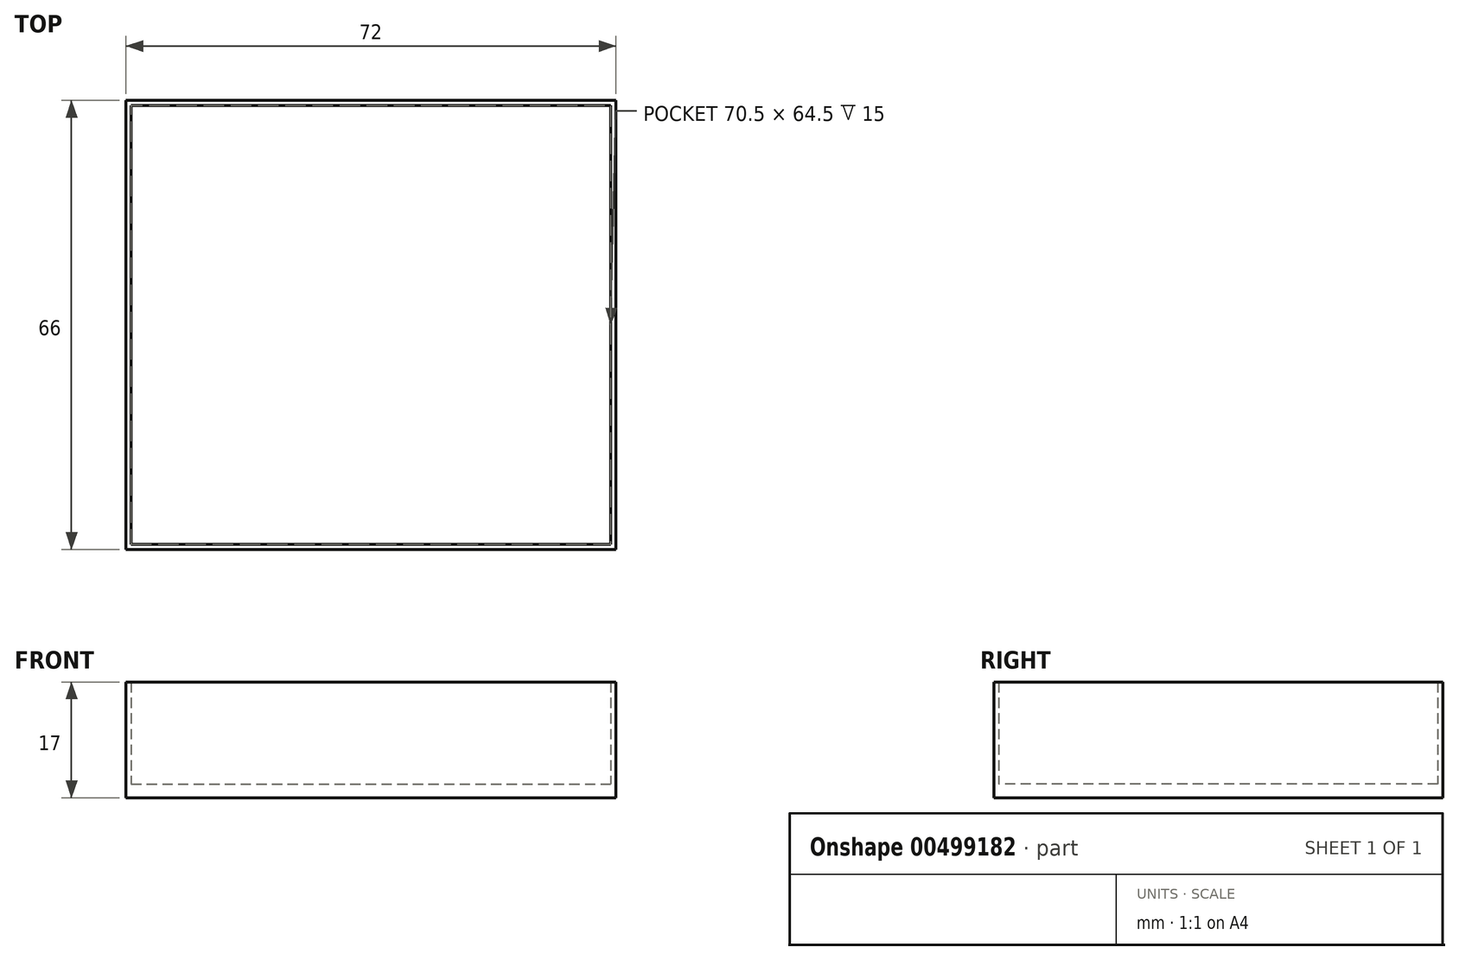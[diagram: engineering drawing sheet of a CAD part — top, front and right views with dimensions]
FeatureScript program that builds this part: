
annotation { "Feature Type Name" : "Feature", "Feature Type Description" : "" }
export const myFeature = defineFeature(function(context is Context, id is Id, definition is map)
    precondition{}
    {
        {
            var Q0;
            Q0=qCreatedBy(makeId("Top.planeOp"),FACE);
            var sketch = newSketch(context, id + "F0", { "sketchPlane" : qUnion([Q0])});
            skLineSegment(sketch, "E0.bottom", {"start": v(-36, 33) * mm, "end": v(36, 33) * mm});
            skLineSegment(sketch, "E0.top", {"start": v(-36, -33) * mm, "end": v(36, -33) * mm});
            skLineSegment(sketch, "E0.left", {"start": v(-36, 33) * mm, "end": v(-36, -33) * mm});
            skLineSegment(sketch, "E0.right", {"start": v(36, 33) * mm, "end": v(36, -33) * mm});
            skPoint(sketch, "E0.middle", {"position": v(0, 0) * mm});
            skSolve(sketch);
        }
        {
            var Q0;
            Q0 = qSketchRegion(id + "F0", true);
            extrude(context, id + "F1", {"entities" : qUnion([Q0]), "depth" : 2 * mm});
        }
        {
            var Q0;
            Q0=makeQuery(id+"F1.opExtrude","CAP_FACE",FACE,{"disambiguationData":[OSD([sQuery(id+"F0.wireOp",EDGE,"E0.bottom"),sQuery(id+"F0.wireOp",EDGE,"E0.top"),sQuery(id+"F0.wireOp",EDGE,"E0.left"),sQuery(id+"F0.wireOp",EDGE,"E0.right")])],"isStart":false});
            var sketch = newSketch(context, id + "F2", { "sketchPlane" : qUnion([Q0])});
            skPoint(sketch, "E1.middle", {"position": v(0, 0) * mm});
            skLineSegment(sketch, "E2.bottom", {"start": v(-36, 33) * mm, "end": v(36, 33) * mm});
            skLineSegment(sketch, "E2.top", {"start": v(-36, -33) * mm, "end": v(36, -33) * mm});
            skLineSegment(sketch, "E2.left", {"start": v(-36, 33) * mm, "end": v(-36, -33) * mm});
            skLineSegment(sketch, "E2.right", {"start": v(36, 33) * mm, "end": v(36, -33) * mm});
            skLineSegment(sketch, "E3.bottom", {"start": v(-35.25, 32.25) * mm, "end": v(35.25, 32.25) * mm});
            skLineSegment(sketch, "E3.top", {"start": v(-35.25, -32.25) * mm, "end": v(35.25, -32.25) * mm});
            skLineSegment(sketch, "E3.left", {"start": v(-35.25, 32.25) * mm, "end": v(-35.25, -32.25) * mm});
            skLineSegment(sketch, "E3.right", {"start": v(35.25, 32.25) * mm, "end": v(35.25, -32.25) * mm});
            skSolve(sketch);
        }
        {
            var Q0;
            Q0=makeQuery(id+"F2.imprint","IMPRINT",FACE,{"disambiguationData":[TD([[makeQuery(id+"F2.imprint","IMPRINT",EDGE,{"derivedFrom":sQuery(id+"F2.wireOp",EDGE,"E2.bottom")}),-1.0]])]});
            extrude(context, id + "F3", {"entities" : qUnion([Q0]), "operationType" : NewBodyOperationType.ADD, "depth" : 15 * mm});
        }
    });
